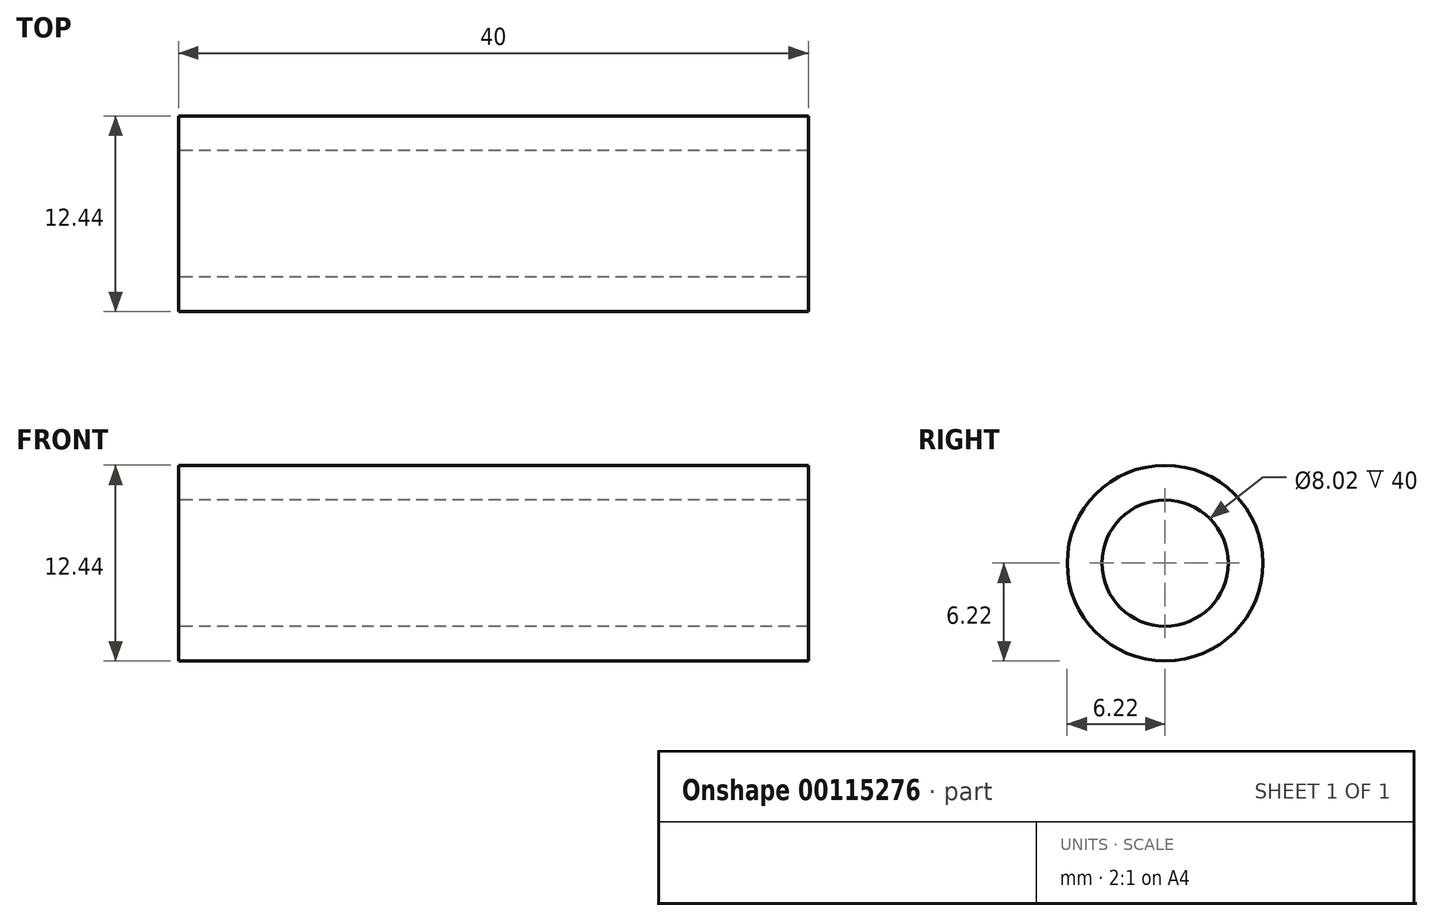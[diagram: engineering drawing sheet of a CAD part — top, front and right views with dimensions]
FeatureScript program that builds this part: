
annotation { "Feature Type Name" : "Feature", "Feature Type Description" : "" }
export const myFeature = defineFeature(function(context is Context, id is Id, definition is map)
    precondition{}
    {
        {
            var Q0;
            Q0=qCreatedBy(makeId("Right.planeOp"),FACE);
            var sketch = newSketch(context, id + "F0", { "sketchPlane" : qUnion([Q0])});
            skCircle(sketch, "E0", {"center": v(-15.95, 17.04) * mm, "radius": 6.64 * mm});
            skSolve(sketch);
        }
        {
            var Q0;
            Q0=makeQuery(id+"F0.imprint","IMPRINT",FACE,{"disambiguationData":[TD([[makeQuery(id+"F0.imprint","IMPRINT",EDGE,{"derivedFrom":sQuery(id+"F0.wireOp",EDGE,"E0")}),1.0]])]});
            var sketch = newSketch(context, id + "F1", { "sketchPlane" : qUnion([Q0])});
            skCircle(sketch, "E1", {"center": v(0, 0) * mm, "radius": 6.22 * mm});
            skCircle(sketch, "E2", {"center": v(0, 0) * mm, "radius": 4 * mm});
            skSolve(sketch);
        }
        {
            var Q0;
            Q0 = qSketchRegion(id + "F1", true);
            var Q1;
            Q1=makeQuery(id+"F1.imprint","IMPRINT",FACE,{"disambiguationData":[TD([[makeQuery(id+"F1.imprint","IMPRINT",EDGE,{"derivedFrom":sQuery(id+"F1.wireOp",EDGE,"E1")}),1.0]])]});
            extrude(context, id + "F2", {"entities" : qUnion([Q0, Q1]), "depth" : 40 * mm});
        }
    });
